# Revit family: Door_StainlessSteel_Ambico_Double-Flush
name_source: partatom
category: Doors
units: mm (PartAtom-declared; Revit-internal decimal feet)

## family parameters
Always vertical = Yes
Classification Number = 23.30.10.14.11
Cut with Voids When Loaded = No
Host = Wall
Room Calculation Point = No
Shared = No

## types (4) — shared parameters
ADA Compliant = Yes
Construction Details = http://www.arcat.com
Frame Finish = Metal - Stainless Steel - Ambico - 2B Finish
Frame Thickness = 0' - 5 7/8"
Frame Width = 0' - 2"
Function = Interior
Green Building-LEED = http://www.arcat.com
Handle Height = 3' - 0"
Hardware Finish = Metal - Stainless Steel - Ambico - 4 Finish
Height = 7' - 0"
Installation-Fabrication = http://www.ambico.com
Keynote = 08300
Manufacturer = Ambico Limited
Manufacturer Fax = 800-465-8561
Manufacturer Website = http://www.ambico.com
Panel Height = 6' - 11 3/4"
Panel Material = Metal - Stainless Steel - Ambico - 2B Finish
Panel Width = 3' - 0"
Product Data = http://www.arcat.com
RO Offset = 0' - 0"
Rough Height = 7' - 0"
Rough Width = 6' - 0"
Sales Information = http://www.ambico.com
Send Message = http://www.arcat.com Limited&coid=40356&rep=119&fax=800-465-8561&mf=
Specification = http://www.arcat.com
Thickness = 0' - 1 3/4"
URL = http://www.ambico.com
Wall Closure = By host
Width = 6' - 0"
ofst = 0' - 0"
zero-valued in all types: Expected Lifespan (Years), Maintenance Schedule (Months), Sound Transmission Class (STC), Warranty Duration (Years)

## per-type parameters (varying)
| type | Description | Fire Rating | Model |
| 304 as Specified | Ambico Stainless Steel Door - Pair as Specified | NFR | Stainless Steel |
| 316 as Specified | Ambico Stainless Steel Door - Pair as Specified | NFR | Stainless Steel |
| 304 Fire Rated as Specified | Ambico Fire Rated Stainless Steel Door - Pair as Specified | 1.5 HR | Stainless Steel Fire Rated |
| 316 Fire Rated as Specified | Ambico Fire Rated Stainless Steel Door - Pair as Specified | 1.5 HR | Stainless Steel Fire Rated |

## geometry (parser evidence)
native form markers: Blend x16, Sweep x12
no freeform markers — native parametric forms only
